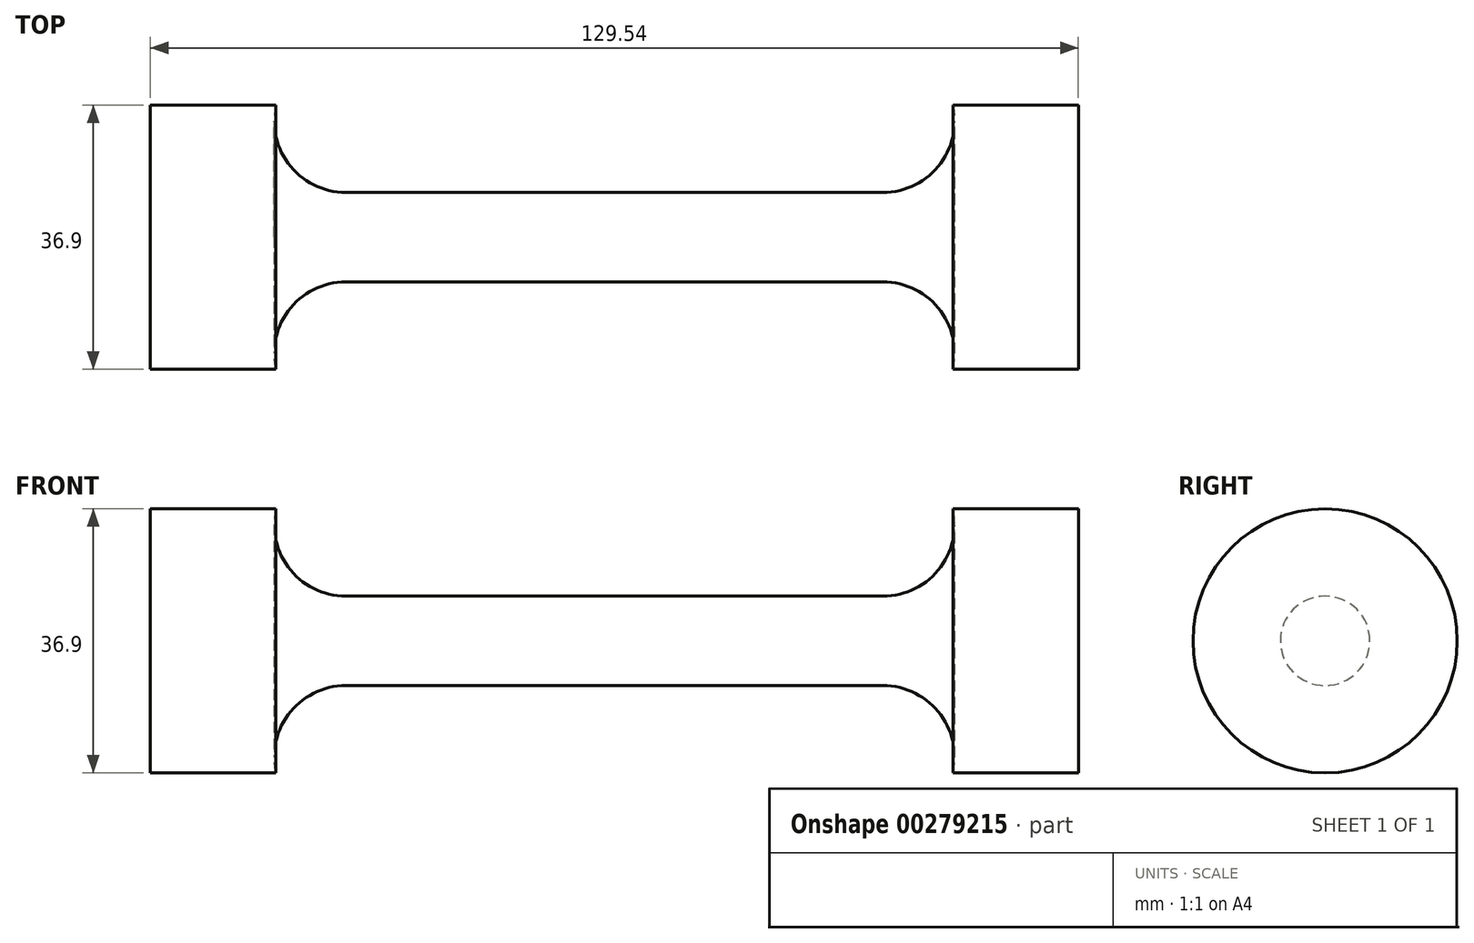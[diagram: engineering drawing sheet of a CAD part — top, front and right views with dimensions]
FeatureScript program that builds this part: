
annotation { "Feature Type Name" : "Feature", "Feature Type Description" : "" }
export const myFeature = defineFeature(function(context is Context, id is Id, definition is map)
    precondition{}
    {
        {
            var Q0;
            Q0=qCreatedBy(makeId("Front.planeOp"),FACE);
            var sketch = newSketch(context, id + "F0", { "sketchPlane" : qUnion([Q0])});
            skLineSegment(sketch, "E0", {"start": v(0, 6.25) * mm, "end": v(37.5, 6.25) * mm});
            skArc(sketch, "E1", {"start": v(37.5, 6.25) * mm, "mid": v(45.3, 10) * mm, "end": v(47.26, 18.45) * mm});
            skLineSegment(sketch, "E2", {"start": v(47.26, 18.45) * mm, "end": v(64.77, 18.45) * mm});
            skLineSegment(sketch, "E3", {"start": v(64.77, 18.45) * mm, "end": v(64.77, 0) * mm});
            skLineSegment(sketch, "E4.MirrorCS", {"start": v(0, 6.25) * mm, "end": v(-37.5, 6.25) * mm});
            skArc(sketch, "E5.MirrorCS", {"start": v(-37.5, 6.25) * mm, "mid": v(-45.3, 10) * mm, "end": v(-47.26, 18.45) * mm});
            skLineSegment(sketch, "E6.MirrorCS", {"start": v(-64.77, 18.45) * mm, "end": v(-64.77, 0) * mm});
            skLineSegment(sketch, "E7.MirrorCS", {"start": v(-47.26, 18.45) * mm, "end": v(-64.77, 18.45) * mm});
            skLineSegment(sketch, "E8", {"start": v(-64.77, 0) * mm, "end": v(64.77, 0) * mm});
            skSolve(sketch);
        }
        {
            var Q0;
            Q0=makeQuery(id+"F0.imprint","IMPRINT",FACE,{"disambiguationData":[TD([[makeQuery(id+"F0.imprint","IMPRINT",EDGE,{"derivedFrom":sQuery(id+"F0.wireOp",EDGE,"E0")}),-1.0]])]});
            var Q1;
            Q1=sQuery(id+"F0.wireOp",EDGE,"E8");
            revolve(context, id + "F1", {"entities" : qUnion([Q0]), "axis" : qUnion([Q1]), "revolveType" : RevolveType.FULL});
        }
    });
